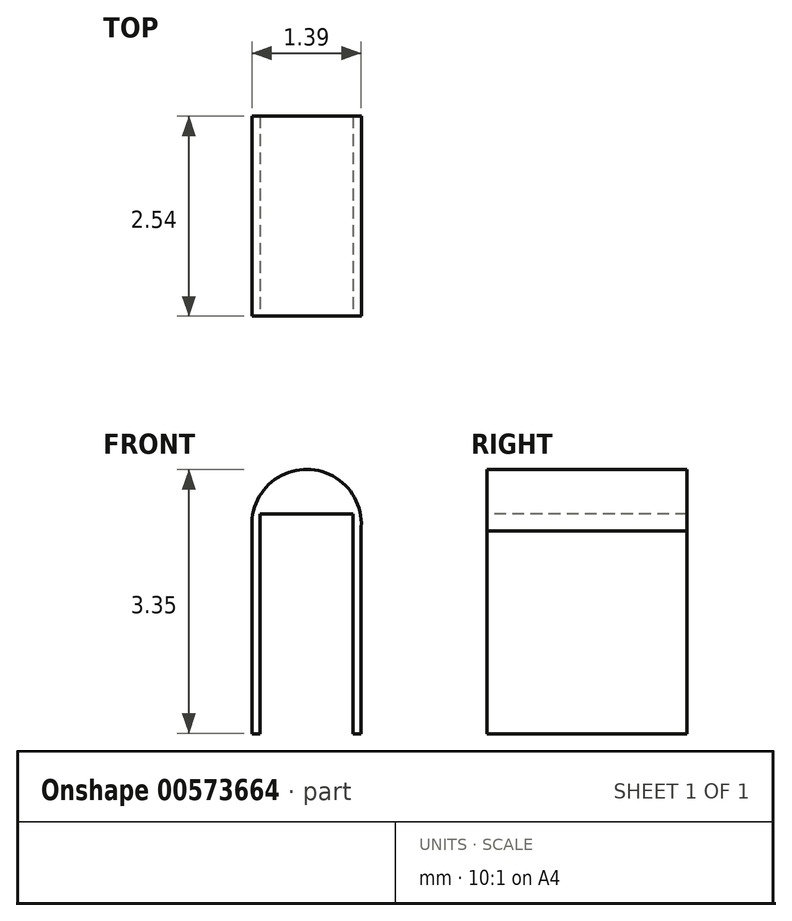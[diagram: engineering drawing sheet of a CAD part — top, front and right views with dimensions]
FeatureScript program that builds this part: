
annotation { "Feature Type Name" : "Feature", "Feature Type Description" : "" }
export const myFeature = defineFeature(function(context is Context, id is Id, definition is map)
    precondition{}
    {
        {
            var Q0;
            Q0=qCreatedBy(makeId("Front.planeOp"),FACE);
            var sketch = newSketch(context, id + "F0", { "sketchPlane" : qUnion([Q0])});
            skArc(sketch, "E0", {"start": v(-3.68, 23.47) * mm, "mid": v(-4.36, 24.25) * mm, "end": v(-5.05, 23.48) * mm});
            skLineSegment(sketch, "E1", {"start": v(-5.05, 23.48) * mm, "end": v(-5.05, 20.9) * mm});
            skLineSegment(sketch, "E2", {"start": v(-3.68, 23.47) * mm, "end": v(-3.68, 20.9) * mm});
            skLineSegment(sketch, "E3", {"start": v(-5.05, 20.9) * mm, "end": v(-3.68, 20.9) * mm});
            skSolve(sketch);
        }
        {
            var Q0;
            Q0 = qSketchRegion(id + "F0", true);
            extrude(context, id + "F1", {"entities" : qUnion([Q0]), "depth" : 2.54 * mm, "offsetDistance" : 25.4 * mm});
        }
        {
            var Q0;
            Q0=makeQuery(id+"F1.opExtrude","SWEPT_FACE",FACE,{"disambiguationData":[OSD([sQuery(id+"F0.wireOp",EDGE,"E3")])]});
            var sketch = newSketch(context, id + "F2", { "sketchPlane" : qUnion([Q0])});
            skLineSegment(sketch, "E4.bottom", {"start": v(-3.78, 0) * mm, "end": v(-4.95, 0) * mm});
            skLineSegment(sketch, "E4.top", {"start": v(-3.78, 2.54) * mm, "end": v(-4.95, 2.54) * mm});
            skLineSegment(sketch, "E4.left", {"start": v(-3.78, 0) * mm, "end": v(-3.78, 2.54) * mm});
            skLineSegment(sketch, "E4.right", {"start": v(-4.95, 0) * mm, "end": v(-4.95, 2.54) * mm});
            skSolve(sketch);
        }
        {
            var Q0;
            Q0 = qSketchRegion(id + "F2", true);
            extrude(context, id + "F3", {"entities" : qUnion([Q0]), "operationType" : NewBodyOperationType.REMOVE, "oppositeDirection" : true, "depth" : 2.8 * mm, "offsetDistance" : 25.4 * mm});
        }
    });
